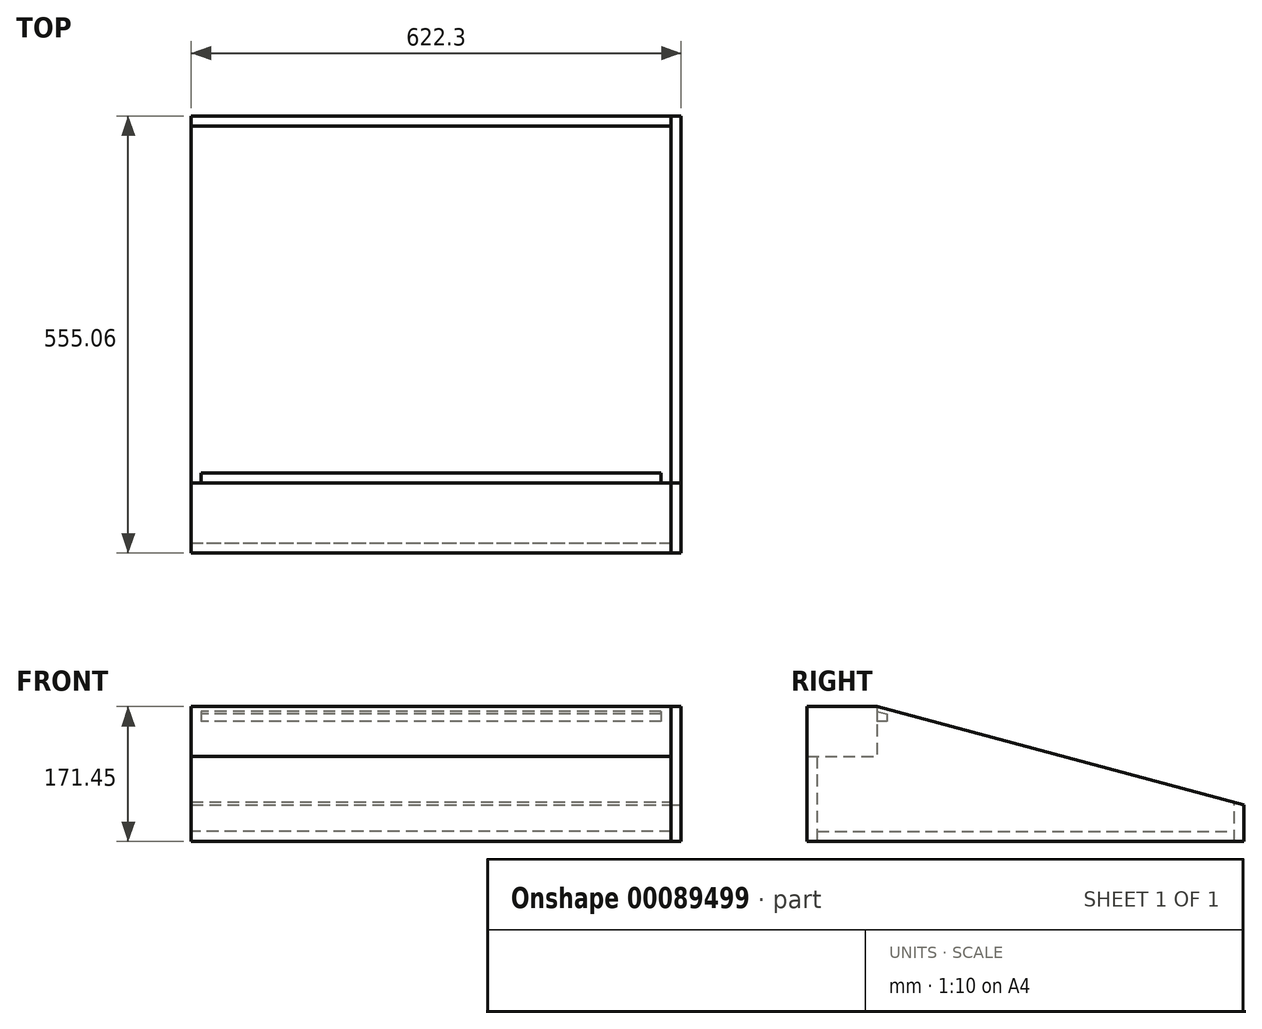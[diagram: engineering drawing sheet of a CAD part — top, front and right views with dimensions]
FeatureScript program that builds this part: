
annotation { "Feature Type Name" : "Feature", "Feature Type Description" : "" }
export const myFeature = defineFeature(function(context is Context, id is Id, definition is map)
    precondition{}
    {
        {
            var Q0;
            Q0=qCreatedBy(makeId("Right.planeOp"),FACE);
            var sketch = newSketch(context, id + "F0", { "sketchPlane" : qUnion([Q0])});
            skLineSegment(sketch, "E0.top", {"start": v(-288.61, 65.37) * mm, "end": v(217.4, 65.37) * mm});
            skLineSegment(sketch, "E0.right", {"start": v(217.4, 18.82) * mm, "end": v(217.4, 65.37) * mm});
            skLineSegment(sketch, "E1", {"start": v(217.4, 65.37) * mm, "end": v(-248.75, 190.27) * mm});
            skLineSegment(sketch, "E2", {"start": v(-248.75, 190.27) * mm, "end": v(-337.65, 190.27) * mm});
            skLineSegment(sketch, "E3", {"start": v(-337.65, 190.27) * mm, "end": v(-337.65, 18.82) * mm});
            skLineSegment(sketch, "E4", {"start": v(-337.65, 18.82) * mm, "end": v(217.4, 18.82) * mm});
            skSolve(sketch);
        }
        {
            var Q0;
            Q0 = qSketchRegion(id + "F0", true);
            extrude(context, id + "F1", {"entities" : qUnion([Q0]), "oppositeDirection" : true, "depth" : 12.7 * mm});
        }
        {
            var Q0;
            Q0=makeQuery(id+"F1.opExtrude","CAP_FACE",FACE,{"disambiguationData":[OSD([sQuery(id+"F0.wireOp",EDGE,"E0.right"),sQuery(id+"F0.wireOp",EDGE,"E1"),sQuery(id+"F0.wireOp",EDGE,"E2"),sQuery(id+"F0.wireOp",EDGE,"E3"),sQuery(id+"F0.wireOp",EDGE,"E4")])],"isStart":false});
            var sketch = newSketch(context, id + "F2", { "sketchPlane" : qUnion([Q0])});
            skLineSegment(sketch, "E5.bottom", {"start": v(-217.4, 18.82) * mm, "end": v(-204.7, 18.82) * mm});
            skLineSegment(sketch, "E5.left", {"start": v(-217.4, 18.82) * mm, "end": v(-217.4, 65.37) * mm});
            skLineSegment(sketch, "E6", {"start": v(-204.7, 18.82) * mm, "end": v(-204.7, 68.77) * mm});
            skLineSegment(sketch, "E7", {"start": v(-204.7, 68.77) * mm, "end": v(-217.4, 65.37) * mm});
            skSolve(sketch);
        }
        {
            var Q0;
            Q0 = qSketchRegion(id + "F2", true);
            extrude(context, id + "F3", {"entities" : qUnion([Q0]), "depth" : 609.6 * mm});
        }
        {
            var Q0;
            Q0=makeQuery(id+"F1.opExtrude","CAP_FACE",FACE,{"disambiguationData":[OSD([sQuery(id+"F0.wireOp",EDGE,"E0.right"),sQuery(id+"F0.wireOp",EDGE,"E1"),sQuery(id+"F0.wireOp",EDGE,"E2"),sQuery(id+"F0.wireOp",EDGE,"E3"),sQuery(id+"F0.wireOp",EDGE,"E4")])],"isStart":false});
            var sketch = newSketch(context, id + "F4", { "sketchPlane" : qUnion([Q0])});
            skLineSegment(sketch, "E8.bottom", {"start": v(337.65, 190.27) * mm, "end": v(248.75, 190.27) * mm});
            skLineSegment(sketch, "E8.top", {"start": v(337.65, 126.77) * mm, "end": v(248.75, 126.77) * mm});
            skLineSegment(sketch, "E8.left", {"start": v(337.65, 190.27) * mm, "end": v(337.65, 126.77) * mm});
            skLineSegment(sketch, "E8.right", {"start": v(248.75, 190.27) * mm, "end": v(248.75, 126.77) * mm});
            skSolve(sketch);
        }
        {
            var Q0;
            Q0=makeQuery(id+"F4.imprint","IMPRINT",FACE,{"disambiguationData":[TD([[makeQuery(id+"F4.imprint","IMPRINT",EDGE,{"derivedFrom":sQuery(id+"F4.wireOp",EDGE,"E8.bottom")}),-1.0]])]});
            extrude(context, id + "F5", {"entities" : qUnion([Q0]), "depth" : 609.6 * mm});
        }
        {
            var Q0;
            Q0=makeQuery(id+"F1.opExtrude","CAP_FACE",FACE,{"disambiguationData":[OSD([sQuery(id+"F0.wireOp",EDGE,"E0.right"),sQuery(id+"F0.wireOp",EDGE,"E1"),sQuery(id+"F0.wireOp",EDGE,"E2"),sQuery(id+"F0.wireOp",EDGE,"E3"),sQuery(id+"F0.wireOp",EDGE,"E4")])],"isStart":false});
            var sketch = newSketch(context, id + "F6", { "sketchPlane" : qUnion([Q0])});
            skLineSegment(sketch, "E9", {"start": v(337.65, 126.77) * mm, "end": v(324.95, 126.77) * mm});
            skLineSegment(sketch, "E10", {"start": v(324.95, 126.77) * mm, "end": v(324.95, 18.82) * mm});
            skLineSegment(sketch, "E11", {"start": v(324.95, 18.82) * mm, "end": v(337.65, 18.82) * mm});
            skLineSegment(sketch, "E12", {"start": v(337.65, 18.82) * mm, "end": v(337.65, 126.77) * mm});
            skSolve(sketch);
        }
        {
            var Q0;
            Q0=makeQuery(id+"F6.imprint","IMPRINT",FACE,{"disambiguationData":[TD([[makeQuery(id+"F6.imprint","IMPRINT",EDGE,{"derivedFrom":sQuery(id+"F6.wireOp",EDGE,"E9")}),1.0]])]});
            extrude(context, id + "F7", {"entities" : qUnion([Q0]), "depth" : 609.6 * mm});
        }
        {
            var Q0;
            Q0=makeQuery(id+"F1.opExtrude","SWEPT_FACE",FACE,{"disambiguationData":[OSD([sQuery(id+"F0.wireOp",EDGE,"E4")])]});
            var sketch = newSketch(context, id + "F8", { "sketchPlane" : qUnion([Q0])});
            skLineSegment(sketch, "E13.bottom", {"start": v(-12.7, 325.25) * mm, "end": v(-622.3, 325.25) * mm});
            skLineSegment(sketch, "E13.top", {"start": v(-12.7, -204.5) * mm, "end": v(-622.3, -204.5) * mm});
            skLineSegment(sketch, "E13.left", {"start": v(-12.7, 325.25) * mm, "end": v(-12.7, -204.5) * mm});
            skLineSegment(sketch, "E13.right", {"start": v(-622.3, 325.25) * mm, "end": v(-622.3, -204.5) * mm});
            skSolve(sketch);
        }
        {
            var Q0;
            Q0 = qSketchRegion(id + "F8", true);
            extrude(context, id + "F9", {"entities" : qUnion([Q0]), "oppositeDirection" : true, "depth" : 12.7 * mm});
        }
        {
            var Q0;
            Q0=makeQuery(id+"F5.opExtrude","SWEPT_FACE",FACE,{"disambiguationData":[OSD([sQuery(id+"F4.wireOp",EDGE,"E8.right")])]});
            var sketch = newSketch(context, id + "F10", { "sketchPlane" : qUnion([Q0])});
            skLineSegment(sketch, "E14.bottom", {"start": v(25.4, 183.92) * mm, "end": v(609.6, 183.92) * mm});
            skLineSegment(sketch, "E14.top", {"start": v(25.4, 171.22) * mm, "end": v(609.6, 171.22) * mm});
            skLineSegment(sketch, "E14.left", {"start": v(25.4, 183.92) * mm, "end": v(25.4, 171.22) * mm});
            skLineSegment(sketch, "E14.right", {"start": v(609.6, 183.92) * mm, "end": v(609.6, 171.22) * mm});
            skSolve(sketch);
        }
        {
            var Q0;
            Q0=makeQuery(id+"F10.imprint","IMPRINT",FACE,{"disambiguationData":[TD([[makeQuery(id+"F10.imprint","IMPRINT",EDGE,{"derivedFrom":sQuery(id+"F10.wireOp",EDGE,"E14.bottom")}),-1.0]])]});
            extrude(context, id + "F11", {"entities" : qUnion([Q0]), "depth" : 12.7 * mm});
        }
        {
            var Q0;
            Q0=makeQuery(id+"F11.opExtrude","SWEPT_FACE",FACE,{"disambiguationData":[OSD([sQuery(id+"F10.wireOp",EDGE,"E14.right")])]});
            var sketch = newSketch(context, id + "F12", { "sketchPlane" : qUnion([Q0])});
            skLineSegment(sketch, "E15", {"start": v(248.75, 171.22) * mm, "end": v(248.75, 183.92) * mm});
            skLineSegment(sketch, "E16", {"start": v(248.75, 183.92) * mm, "end": v(236.05, 180.52) * mm});
            skLineSegment(sketch, "E17", {"start": v(236.05, 180.52) * mm, "end": v(236.05, 183.92) * mm});
            skLineSegment(sketch, "E18", {"start": v(236.05, 183.92) * mm, "end": v(248.75, 183.92) * mm});
            skSolve(sketch);
        }
        {
            var Q0;
            Q0=makeQuery(id+"F12.imprint","IMPRINT",FACE,{"disambiguationData":[TD([[makeQuery(id+"F12.imprint","IMPRINT",EDGE,{"derivedFrom":sQuery(id+"F12.wireOp",EDGE,"E16")}),-1.0]])]});
            extrude(context, id + "F13", {"entities" : qUnion([Q0]), "operationType" : NewBodyOperationType.REMOVE, "endBound" : BoundingType.UP_TO_NEXT, "oppositeDirection" : true, "depth" : 25.4 * mm});
        }
    });
